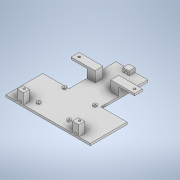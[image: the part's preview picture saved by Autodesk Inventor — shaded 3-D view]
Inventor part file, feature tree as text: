
AUTODESK INVENTOR PART (.ipt)
format: ipt  version: 2020 (Build 240168000, 168)  size: 265,216 bytes
history: native  units: mm
features: sketch x10, extrude x6, hole x5, mirror x1
ambient origin geometry x8: Origin, YZ Plane, XZ Plane, XY Plane, X Axis, Y Axis, Z Axis, Center Point
bodies: Solid1 (feature_tree)
feature tree (22):
  extrude  "Extrusion1"  Depth=30.0mm
  sketch  "Sketch2"  dims[d2=50.0mm d3=70.0mm]
  extrude  "Extrusion2"  Depth=70.0mm
  extrude  "Extrusion4"  Depth=12.0mm
  extrude  "Extrusion5"  Depth=6.0mm
  extrude  "Extrusion6"  Depth=6.0mm
  hole  "Hole5"  [1 undecoded]
  mirror  "Mirror1"
  extrude  "Extrusion3"  Depth=8.0mm
  hole  "Hole3"  [1 undecoded]
  hole  "Hole2"  [1 undecoded]
  hole  "Hole1"  [1 undecoded]
  hole  "Hole4"  [1 undecoded]
  sketch  "Sketch1"  dims[d0=159.0mm d1=30.0mm]
  sketch  "Sketch3"  dims[d4=4.0mm d5=0.0mm d6=12.0mm]
  sketch  "Sketch4"  dims[d7=11.0mm d8=6.0mm]
  sketch  "Sketch5"  dims[d9=8.0mm d10=0.0mm d11=6.0mm]
  sketch  "Sketch6"  dims[d12=6.0mm]
  sketch  "Sketch7"  dims[d13=5.9mm d14=6.0mm d15=4.0mm d16=2.0mm d17=90.0deg d18=8.0mm d19=0.0mm d21=6.0mm]
  sketch  "Sketch9"  dims[d22=6.0mm]
  sketch  "Sketch10"  dims[d24=5.9mm d25=6.0mm d26=4.0mm d27=2.0mm d28=90.0deg d29=8.0mm d30=0.0mm d31=58.0mm]
  sketch  "Sketch11"  dims[d32=49.0mm d33=7.0mm d34=2.0mm d35=0.0mm d36=1.8mm d37=6.0mm d38=4.0mm d39=2.0mm d40=90.0deg d41=8.0mm d42=0.0mm d45=42.0mm d50=20.0mm d51=0.0mm d52=46.5mm d53=6.0mm d54=6.0mm d55=4.1mm d56=6.0mm d57=4.0mm d58=2.0mm d59=90.0deg d60=6.0mm d61=0.0mm d63=111.5mm d64=15.0mm d65=15.0mm d66=20.0mm d67=0.0mm d68=4.0mm d69=30.0mm d70=0.0mm d71=7.5mm d72=4.6mm d73=6.0mm d74=4.0mm d75=2.0mm d76=90.0deg d77=6.0mm d78=0.0mm d79=13.0mm d80=7.0mm d81=7.0mm d82=7.5mm]
note: 5 required parameter values undecoded (feature->parameter linkage not recoverable at this tier; creation-order binding heuristic only, values carry confidence <= 0.55)
